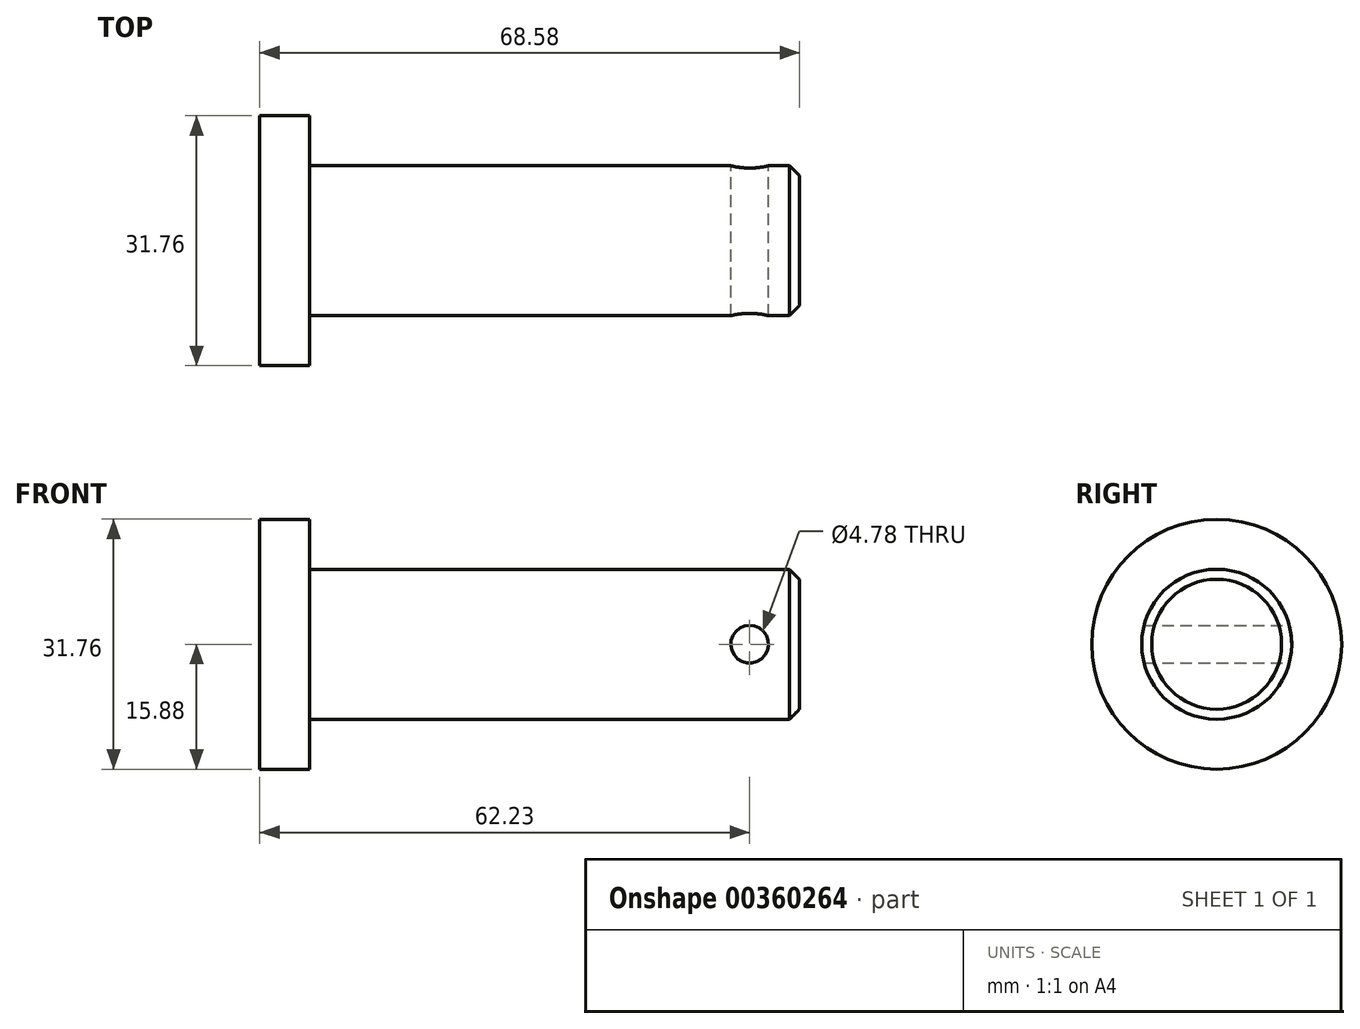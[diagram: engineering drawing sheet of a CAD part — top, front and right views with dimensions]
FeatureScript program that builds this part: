
annotation { "Feature Type Name" : "Feature", "Feature Type Description" : "" }
export const myFeature = defineFeature(function(context is Context, id is Id, definition is map)
    precondition{}
    {
        {
            var Q0;
            Q0=qCreatedBy(makeId("Right.planeOp"),FACE);
            var sketch = newSketch(context, id + "F0", { "sketchPlane" : qUnion([Q0])});
            skCircle(sketch, "E0", {"center": v(0, 0) * mm, "radius": 15.88 * mm});
            skCircle(sketch, "E1", {"center": v(0, 0) * mm, "radius": 9.53 * mm});
            skSolve(sketch);
        }
        {
            var Q0;
            Q0=makeQuery(id+"F0.imprint","IMPRINT",FACE,{"disambiguationData":[TD([[makeQuery(id+"F0.imprint","IMPRINT",EDGE,{"derivedFrom":sQuery(id+"F0.wireOp",EDGE,"E0")}),1.0]])]});
            extrude(context, id + "F1", {"entities" : qUnion([Q0]), "depth" : 6.35 * mm});
        }
        {
            var Q0;
            Q0=makeQuery(id+"F0.imprint","IMPRINT",FACE,{"disambiguationData":[TD([[makeQuery(id+"F0.imprint","IMPRINT",EDGE,{"derivedFrom":sQuery(id+"F0.wireOp",EDGE,"E1")}),1.0]])]});
            extrude(context, id + "F2", {"entities" : qUnion([Q0]), "operationType" : NewBodyOperationType.ADD, "depth" : 68.58 * mm});
        }
        {
            var Q0;
            Q0=qCreatedBy(makeId("Front.planeOp"),FACE);
            var sketch = newSketch(context, id + "F3", { "sketchPlane" : qUnion([Q0])});
            skLineSegment(sketch, "E2", {"start": v(0, 0) * mm, "end": v(77.05, 0) * mm, "construction": true});
            skCircle(sketch, "E3", {"center": v(62.23, 0) * mm, "radius": 2.39 * mm});
            skSolve(sketch);
        }
        {
            var Q0;
            Q0 = qSketchRegion(id + "F3", true);
            extrude(context, id + "F4", {"entities" : qUnion([Q0]), "operationType" : NewBodyOperationType.REMOVE, "endBound" : BoundingType.SYMMETRIC, "depth" : 25.4 * mm});
        }
        {
            var Q0;
            Q0=makeQuery(id+"F2.opExtrude","CAP_EDGE",EDGE,{"disambiguationData":[OSD([sQuery(id+"F0.wireOp",EDGE,"E1")])],"isStart":false});
            chamfer(context, id + "F5", {"entities" : qUnion([Q0]), "chamferType" : ChamferType.OFFSET_ANGLE, "width" : 1.27 * mm, "oppositeDirection" : false, "angle" : 45 * degree, "tangentPropagation" : true});
        }
    });
